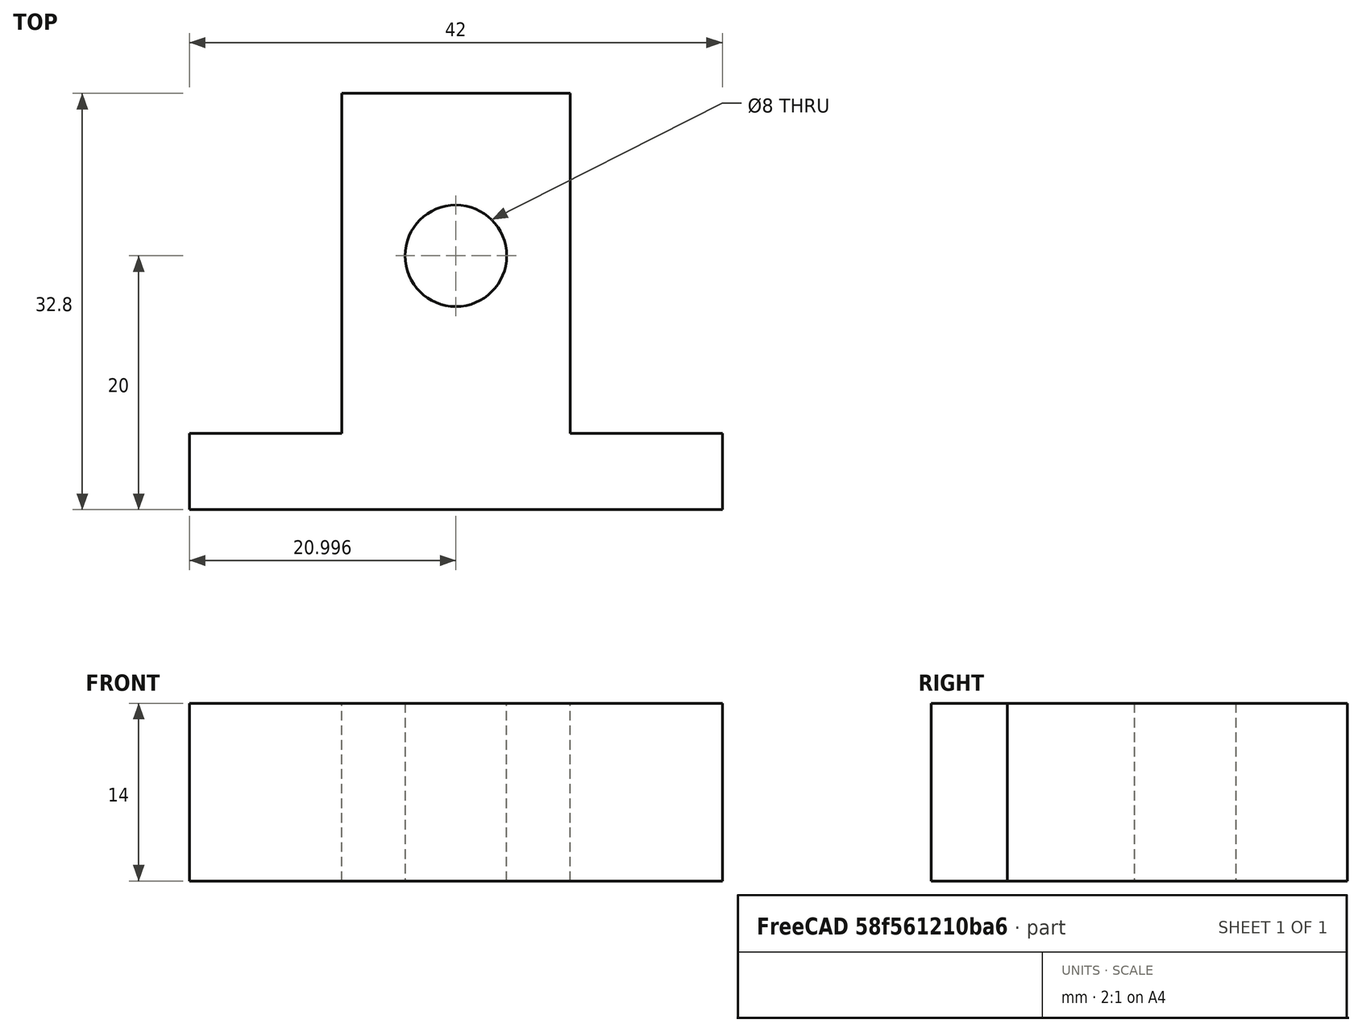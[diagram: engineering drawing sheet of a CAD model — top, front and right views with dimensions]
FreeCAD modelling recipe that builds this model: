
FCSTD DOCUMENT  (FreeCAD 0.14R3702 (Git))
Label: 8mm_rail_support_guide
License: CC-BY 3.0
LicenseURL: http://creativecommons.org/licenses/by/3.0/
objects: Sketcher::SketchObject×1, PartDesign::Pad×1
note: 3 computed .brp shape members not serialized (recipe doc carries the construction recipe); baked Part::Feature solids carry a one-line shape summary decoded from their .brp

FEATURE [Sketcher::SketchObject] Sketch
  sketch-geometry (9):
    g0: LineSegment StartX=-21 StartY=0 StartZ=0 EndX=21 EndY=0 EndZ=0
    g1: LineSegment StartX=21 StartY=0 StartZ=0 EndX=21 EndY=6 EndZ=0
    g2: LineSegment StartX=21 StartY=6 StartZ=0 EndX=9 EndY=6 EndZ=0
    g3: LineSegment StartX=9 StartY=6 StartZ=0 EndX=9 EndY=32.8 EndZ=0
    g4: LineSegment StartX=9 StartY=32.8 StartZ=0 EndX=-9 EndY=32.8 EndZ=0
    g5: LineSegment StartX=-9 StartY=32.8 StartZ=0 EndX=-9 EndY=6 EndZ=0
    g6: LineSegment StartX=-9 StartY=6 StartZ=0 EndX=-21 EndY=6 EndZ=0
    g7: LineSegment StartX=-21 StartY=6 StartZ=0 EndX=-21 EndY=0 EndZ=0
    g8: Circle CenterX=-0.00411 CenterY=20 CenterZ=0 NormalX=0 NormalY=0 NormalZ=1 Radius=4
  constraints (27):
    c: PointOnObject(g0,g-1)
    c: PointOnObject(g0,g-1)
    c: Coincident(g1,g0)
    c: Vertical(g1)
    c: Coincident(g2,g1)
    c: Horizontal(g2)
    c: Coincident(g3,g2)
    c: Vertical(g3)
    c: Coincident(g4,g3)
    c: Horizontal(g4)
    c: Coincident(g5,g4)
    c: Vertical(g5)
    c: Coincident(g6,g5)
    c: Horizontal(g6)
    c: Coincident(g7,g6)
    c: Coincident(g7,g0)
    c: Vertical(g7)
    c: Distance(g0) = 42
    c: Distance(g7) = 6
    c: Equal(g7,g1)
    c: Distance(g4) = 18
    c: Distance(g6) = 12
    c: Equal(g6,g2)
    c: Symmetric(g0,g0,g-1)
    c: Distance(g3) = 26.8
    c: Radius(g8) = 4
    c: Distance(g8,g0) = 20
FEATURE [PartDesign::Pad] Pad  label="8mm_rail_support_guide"
  Length = 14
  Length2 = 10
  Sketch = -> Sketch
  Type = 0
